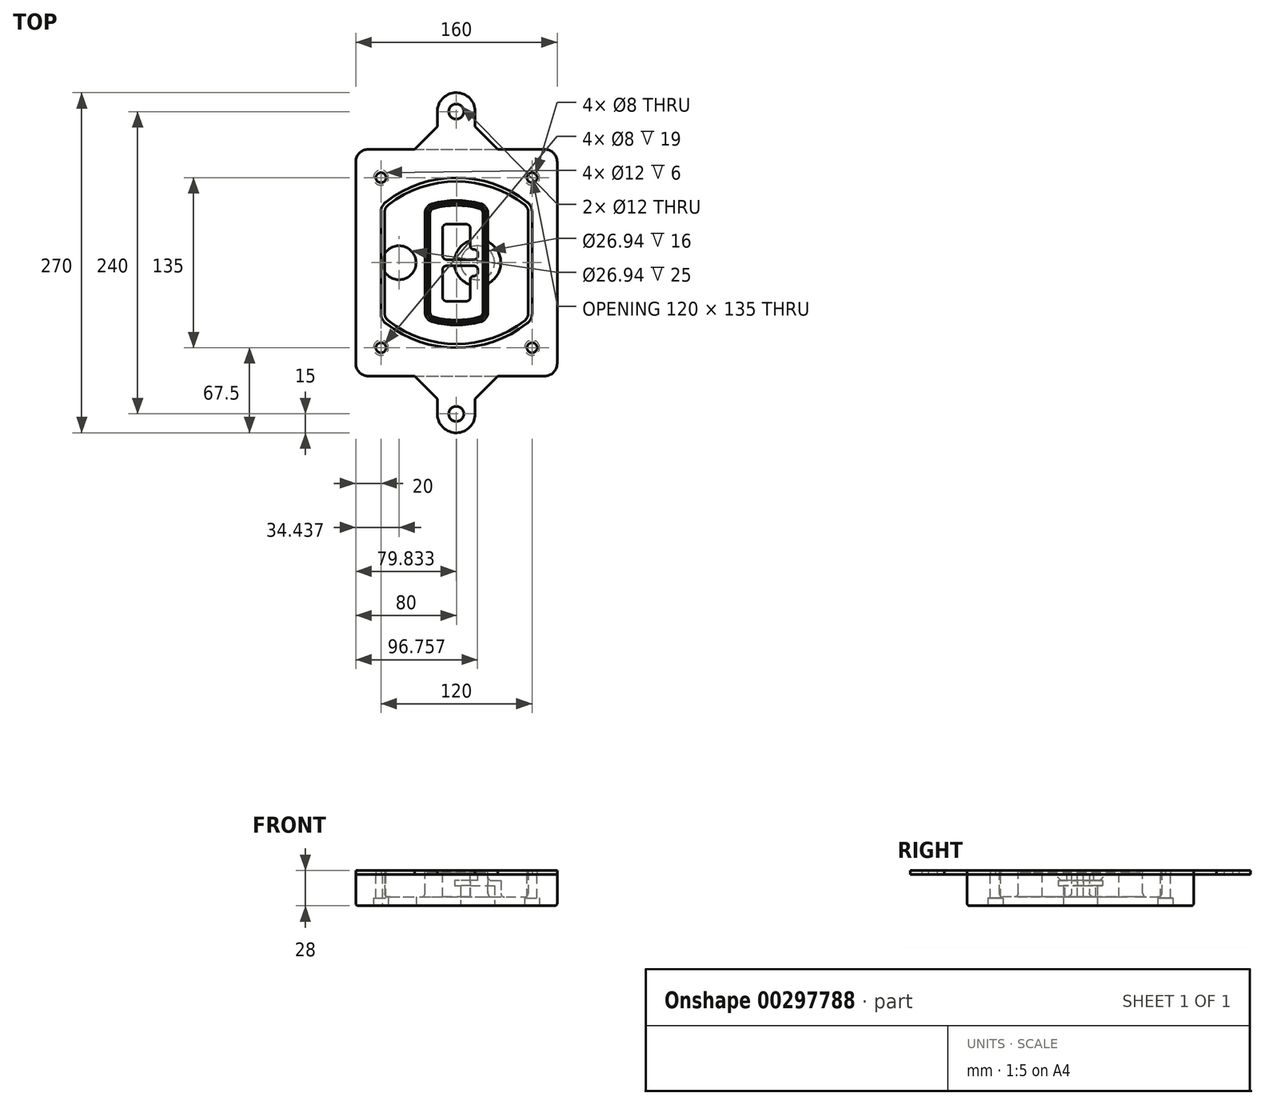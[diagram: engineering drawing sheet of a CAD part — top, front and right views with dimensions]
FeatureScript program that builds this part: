
annotation { "Feature Type Name" : "Feature", "Feature Type Description" : "" }
export const myFeature = defineFeature(function(context is Context, id is Id, definition is map)
    precondition{}
    {
        {
            var Q0;
            Q0=qCreatedBy(makeId("Top.planeOp"),FACE);
            var sketch = newSketch(context, id + "F0", { "sketchPlane" : qUnion([Q0])});
            skPoint(sketch, "E0.rect.middle", {"position": v(0, 0) * mm});
            skLineSegment(sketch, "E1.bottom", {"start": v(-70, -90) * mm, "end": v(70, -90) * mm});
            skLineSegment(sketch, "E1.top", {"start": v(-70, 90) * mm, "end": v(70, 90) * mm});
            skLineSegment(sketch, "E1.left", {"start": v(-80, -80) * mm, "end": v(-80, 80) * mm});
            skLineSegment(sketch, "E1.right", {"start": v(80, -80) * mm, "end": v(80, 80) * mm});
            skLineSegment(sketch, "E2", {"start": v(-80, 90) * mm, "end": v(80, -90) * mm, "construction": true});
            skLineSegment(sketch, "E3", {"start": v(80, 90) * mm, "end": v(-80, -90) * mm, "construction": true});
            skCircle(sketch, "E4", {"center": v(-60, 67.5) * mm, "radius": 4 * mm});
            skCircle(sketch, "E5", {"center": v(60, 67.5) * mm, "radius": 4 * mm});
            skCircle(sketch, "E6", {"center": v(60, -67.5) * mm, "radius": 4 * mm});
            skCircle(sketch, "E7", {"center": v(-60, -67.5) * mm, "radius": 4 * mm});
            skLineSegment(sketch, "E8", {"start": v(-60, 67.5) * mm, "end": v(60, 67.5) * mm, "construction": true});
            skLineSegment(sketch, "E9", {"start": v(60, 67.5) * mm, "end": v(60, -67.5) * mm, "construction": true});
            skLineSegment(sketch, "E10", {"start": v(60, -67.5) * mm, "end": v(-60, -67.5) * mm, "construction": true});
            skLineSegment(sketch, "E11", {"start": v(-60, -67.5) * mm, "end": v(-60, 67.5) * mm, "construction": true});
            skLineSegment(sketch, "E12", {"start": v(-60, 40.3) * mm, "end": v(-60, -40.3) * mm});
            skLineSegment(sketch, "E13", {"start": v(60, 40.3) * mm, "end": v(60, -40.3) * mm});
            skArc(sketch, "E14", {"start": v(56.15, 48.18) * mm, "mid": v(0, 67.5) * mm, "end": v(-56.15, 48.18) * mm});
            skArc(sketch, "E15", {"start": v(-56.15, -48.18) * mm, "mid": v(0, -67.5) * mm, "end": v(56.15, -48.18) * mm});
            skLineSegment(sketch, "E16", {"start": v(-60, 0) * mm, "end": v(60, 0) * mm, "construction": true});
            skPoint(sketch, "E17.visualSharp", {"position": v(-60, -45) * mm});
            skArc(sketch, "E17.filletArc", {"start": v(-60, -40.3) * mm, "mid": v(-58.99, -44.68) * mm, "end": v(-56.15, -48.18) * mm});
            skPoint(sketch, "E18.visualSharp", {"position": v(-60, 45) * mm});
            skArc(sketch, "E18.filletArc", {"start": v(-56.15, 48.18) * mm, "mid": v(-58.99, 44.68) * mm, "end": v(-60, 40.3) * mm});
            skPoint(sketch, "E19.visualSharp", {"position": v(60, 45) * mm});
            skArc(sketch, "E19.filletArc", {"start": v(60, 40.3) * mm, "mid": v(58.99, 44.68) * mm, "end": v(56.15, 48.18) * mm});
            skPoint(sketch, "E20.visualSharp", {"position": v(60, -45) * mm});
            skArc(sketch, "E20.filletArc", {"start": v(56.15, -48.18) * mm, "mid": v(58.99, -44.68) * mm, "end": v(60, -40.3) * mm});
            skPoint(sketch, "E21.visualSharp", {"position": v(-80, 90) * mm});
            skArc(sketch, "E21.filletArc", {"start": v(-70, 90) * mm, "mid": v(-77.07, 87.07) * mm, "end": v(-80, 80) * mm});
            skPoint(sketch, "E22.visualSharp", {"position": v(80, 90) * mm});
            skArc(sketch, "E22.filletArc", {"start": v(80, 80) * mm, "mid": v(77.07, 87.07) * mm, "end": v(70, 90) * mm});
            skPoint(sketch, "E23.visualSharp", {"position": v(80, -90) * mm});
            skArc(sketch, "E23.filletArc", {"start": v(70, -90) * mm, "mid": v(77.07, -87.07) * mm, "end": v(80, -80) * mm});
            skPoint(sketch, "E24.visualSharp", {"position": v(-80, -90) * mm});
            skArc(sketch, "E24.filletArc", {"start": v(-80, -80) * mm, "mid": v(-77.07, -87.07) * mm, "end": v(-70, -90) * mm});
            skArc(sketch, "E25.0", {"start": v(57, 40.3) * mm, "mid": v(56.3, 43.36) * mm, "end": v(54.3, 45.81) * mm});
            skLineSegment(sketch, "E25.1", {"start": v(57, 40.3) * mm, "end": v(57, -40.3) * mm});
            skArc(sketch, "E25.2", {"start": v(54.3, -45.81) * mm, "mid": v(56.3, -43.36) * mm, "end": v(57, -40.3) * mm});
            skArc(sketch, "E25.3", {"start": v(-54.3, -45.81) * mm, "mid": v(0, -64.5) * mm, "end": v(54.3, -45.81) * mm});
            skArc(sketch, "E25.4", {"start": v(-57, -40.3) * mm, "mid": v(-56.3, -43.36) * mm, "end": v(-54.3, -45.81) * mm});
            skArc(sketch, "E25.5", {"start": v(54.3, 45.81) * mm, "mid": v(0, 64.5) * mm, "end": v(-54.3, 45.81) * mm});
            skLineSegment(sketch, "E25.6", {"start": v(-57, 40.3) * mm, "end": v(-57, -40.3) * mm});
            skArc(sketch, "E25.7", {"start": v(-54.3, 45.81) * mm, "mid": v(-56.3, 43.36) * mm, "end": v(-57, 40.3) * mm});
            skArc(sketch, "E26.0", {"start": v(-58.62, 51.33) * mm, "mid": v(-62.58, 46.43) * mm, "end": v(-64, 40.3) * mm});
            skArc(sketch, "E26.1", {"start": v(58.62, 51.33) * mm, "mid": v(0, 71.5) * mm, "end": v(-58.62, 51.33) * mm});
            skArc(sketch, "E26.2", {"start": v(64, 40.3) * mm, "mid": v(62.58, 46.43) * mm, "end": v(58.62, 51.33) * mm});
            skLineSegment(sketch, "E26.3", {"start": v(64, 40.3) * mm, "end": v(64, -40.3) * mm});
            skArc(sketch, "E26.4", {"start": v(58.62, -51.33) * mm, "mid": v(62.58, -46.43) * mm, "end": v(64, -40.3) * mm});
            skLineSegment(sketch, "E26.5", {"start": v(-64, 40.3) * mm, "end": v(-64, -40.3) * mm});
            skArc(sketch, "E26.6", {"start": v(-58.62, -51.33) * mm, "mid": v(0, -71.5) * mm, "end": v(58.62, -51.33) * mm});
            skArc(sketch, "E26.7", {"start": v(-64, -40.3) * mm, "mid": v(-62.58, -46.43) * mm, "end": v(-58.62, -51.33) * mm});
            skSolve(sketch);
        }
        {
            var Q0;
            Q0=makeQuery(id+"F0.imprint","IMPRINT",FACE,{"disambiguationData":[TD([[makeQuery(id+"F0.imprint","IMPRINT",EDGE,{"derivedFrom":sQuery(id+"F0.wireOp",EDGE,"E1.bottom")}),1.0]])]});
            var Q1;
            Q1=makeQuery(id+"F0.imprint","IMPRINT",FACE,{"disambiguationData":[TD([[makeQuery(id+"F0.imprint","IMPRINT",EDGE,{"derivedFrom":sQuery(id+"F0.wireOp",EDGE,"E12")}),1.0]])]});
            var Q2;
            Q2=makeQuery(id+"F0.imprint","IMPRINT",FACE,{"disambiguationData":[TD([[makeQuery(id+"F0.imprint","IMPRINT",EDGE,{"derivedFrom":sQuery(id+"F0.wireOp",EDGE,"E25.0")}),1.0]])]});
            var Q3;
            Q3=makeQuery(id+"F0.imprint","IMPRINT",FACE,{"disambiguationData":[TD([[makeQuery(id+"F0.imprint","IMPRINT",EDGE,{"derivedFrom":sQuery(id+"F0.wireOp",EDGE,"E12")}),-1.0]])]});
            extrude(context, id + "F1", {"entities" : qUnion([Q0, Q1, Q2, Q3]), "oppositeDirection" : true, "depth" : 25 * mm});
        }
        {
            var Q0;
            Q0=makeQuery(id+"F0.imprint","IMPRINT",FACE,{"disambiguationData":[TD([[makeQuery(id+"F0.imprint","IMPRINT",EDGE,{"derivedFrom":sQuery(id+"F0.wireOp",EDGE,"E12")}),1.0]])]});
            extrude(context, id + "F2", {"entities" : qUnion([Q0]), "operationType" : NewBodyOperationType.ADD, "depth" : 3 * mm});
        }
        {
            var Q0;
            Q0=makeQuery(id+"F0.imprint","IMPRINT",FACE,{"disambiguationData":[TD([[makeQuery(id+"F0.imprint","IMPRINT",EDGE,{"derivedFrom":sQuery(id+"F0.wireOp",EDGE,"E25.0")}),1.0]])]});
            extrude(context, id + "F3", {"entities" : qUnion([Q0]), "operationType" : NewBodyOperationType.REMOVE, "oppositeDirection" : true, "depth" : 18 * mm});
        }
        {
            var Q0;
            Q0=makeQuery(id+"F2.opExtrude","CAP_FACE",FACE,{"disambiguationData":[OSD([sQuery(id+"F0.wireOp",EDGE,"E12"),sQuery(id+"F0.wireOp",EDGE,"E13"),sQuery(id+"F0.wireOp",EDGE,"E14"),sQuery(id+"F0.wireOp",EDGE,"E15"),sQuery(id+"F0.wireOp",EDGE,"E17.filletArc"),sQuery(id+"F0.wireOp",EDGE,"E18.filletArc"),sQuery(id+"F0.wireOp",EDGE,"E19.filletArc"),sQuery(id+"F0.wireOp",EDGE,"E20.filletArc"),sQuery(id+"F0.wireOp",EDGE,"E25.0"),sQuery(id+"F0.wireOp",EDGE,"E25.1"),sQuery(id+"F0.wireOp",EDGE,"E25.2"),sQuery(id+"F0.wireOp",EDGE,"E25.3"),sQuery(id+"F0.wireOp",EDGE,"E25.4"),sQuery(id+"F0.wireOp",EDGE,"E25.5"),sQuery(id+"F0.wireOp",EDGE,"E25.6"),sQuery(id+"F0.wireOp",EDGE,"E25.7")])],"isStart":false});
            var sketch = newSketch(context, id + "F4", { "sketchPlane" : qUnion([Q0])});
            skArc(sketch, "E27.0", {"start": v(-19.08, -46.97) * mm, "mid": v(0, -49.5) * mm, "end": v(19.08, -46.97) * mm});
            skArc(sketch, "E28.0", {"start": v(19.08, 46.97) * mm, "mid": v(0, 49.5) * mm, "end": v(-19.08, 46.97) * mm});
            skLineSegment(sketch, "E29", {"start": v(-25, 39.25) * mm, "end": v(-25, -39.25) * mm});
            skLineSegment(sketch, "E30", {"start": v(25, 39.25) * mm, "end": v(25, -39.25) * mm});
            skLineSegment(sketch, "E31", {"start": v(-25, 45.1) * mm, "end": v(25, 45.1) * mm, "construction": true});
            skLineSegment(sketch, "E32", {"start": v(-25, -45.1) * mm, "end": v(25, -45.1) * mm, "construction": true});
            skPoint(sketch, "E33.visualSharp", {"position": v(-25, 45.1) * mm});
            skArc(sketch, "E33.filletArc", {"start": v(-19.08, 46.97) * mm, "mid": v(-23.35, 44.11) * mm, "end": v(-25, 39.25) * mm});
            skPoint(sketch, "E34.visualSharp", {"position": v(25, 45.1) * mm});
            skArc(sketch, "E34.filletArc", {"start": v(25, 39.25) * mm, "mid": v(23.35, 44.11) * mm, "end": v(19.08, 46.97) * mm});
            skPoint(sketch, "E35.visualSharp", {"position": v(25, -45.1) * mm});
            skArc(sketch, "E35.filletArc", {"start": v(19.08, -46.97) * mm, "mid": v(23.35, -44.11) * mm, "end": v(25, -39.25) * mm});
            skPoint(sketch, "E36.visualSharp", {"position": v(-25, -45.1) * mm});
            skArc(sketch, "E36.filletArc", {"start": v(-25, -39.25) * mm, "mid": v(-23.35, -44.11) * mm, "end": v(-19.08, -46.97) * mm});
            skArc(sketch, "E37.0", {"start": v(54.3, 45.81) * mm, "mid": v(0, 64.5) * mm, "end": v(-54.3, 45.81) * mm});
            skArc(sketch, "E37.1", {"start": v(-54.3, 45.81) * mm, "mid": v(-56.3, 43.36) * mm, "end": v(-57, 40.3) * mm});
            skLineSegment(sketch, "E37.2", {"start": v(-57, 40.3) * mm, "end": v(-57, -40.3) * mm});
            skArc(sketch, "E37.3", {"start": v(-57, -40.3) * mm, "mid": v(-56.3, -43.36) * mm, "end": v(-54.3, -45.81) * mm});
            skArc(sketch, "E37.4", {"start": v(-54.3, -45.81) * mm, "mid": v(0, -64.5) * mm, "end": v(54.3, -45.81) * mm});
            skArc(sketch, "E37.5", {"start": v(54.3, -45.81) * mm, "mid": v(56.3, -43.36) * mm, "end": v(57, -40.3) * mm});
            skLineSegment(sketch, "E37.6", {"start": v(57, 40.3) * mm, "end": v(57, -40.3) * mm});
            skArc(sketch, "E37.7", {"start": v(57, 40.3) * mm, "mid": v(56.3, 43.36) * mm, "end": v(54.3, 45.81) * mm});
            skLineSegment(sketch, "E38.0", {"start": v(23, 39.25) * mm, "end": v(23, -39.25) * mm});
            skArc(sketch, "E38.1", {"start": v(18.56, -45.04) * mm, "mid": v(21.76, -42.9) * mm, "end": v(23, -39.25) * mm});
            skArc(sketch, "E38.2", {"start": v(-18.56, -45.04) * mm, "mid": v(0, -47.5) * mm, "end": v(18.56, -45.04) * mm});
            skArc(sketch, "E38.3", {"start": v(-23, -39.25) * mm, "mid": v(-21.76, -42.9) * mm, "end": v(-18.56, -45.04) * mm});
            skLineSegment(sketch, "E38.4", {"start": v(-23, 39.25) * mm, "end": v(-23, -39.25) * mm});
            skArc(sketch, "E38.5", {"start": v(23, 39.25) * mm, "mid": v(21.76, 42.9) * mm, "end": v(18.56, 45.04) * mm});
            skArc(sketch, "E38.6", {"start": v(-18.56, 45.04) * mm, "mid": v(-21.76, 42.9) * mm, "end": v(-23, 39.25) * mm});
            skArc(sketch, "E38.7", {"start": v(18.56, 45.04) * mm, "mid": v(0, 47.5) * mm, "end": v(-18.56, 45.04) * mm});
            skArc(sketch, "E39.0", {"start": v(21, 39.25) * mm, "mid": v(20.18, 41.68) * mm, "end": v(18.04, 43.1) * mm});
            skLineSegment(sketch, "E39.1", {"start": v(21, 39.25) * mm, "end": v(21, -39.25) * mm});
            skArc(sketch, "E39.2", {"start": v(18.04, -43.1) * mm, "mid": v(20.18, -41.68) * mm, "end": v(21, -39.25) * mm});
            skArc(sketch, "E39.3", {"start": v(-18.04, -43.1) * mm, "mid": v(0, -45.5) * mm, "end": v(18.04, -43.1) * mm});
            skArc(sketch, "E39.4", {"start": v(-21, -39.25) * mm, "mid": v(-20.18, -41.68) * mm, "end": v(-18.04, -43.1) * mm});
            skArc(sketch, "E39.5", {"start": v(18.04, 43.1) * mm, "mid": v(0, 45.5) * mm, "end": v(-18.04, 43.1) * mm});
            skLineSegment(sketch, "E39.6", {"start": v(-21, 39.25) * mm, "end": v(-21, -39.25) * mm});
            skArc(sketch, "E39.7", {"start": v(-18.04, 43.1) * mm, "mid": v(-20.18, 41.68) * mm, "end": v(-21, 39.25) * mm});
            skLineSegment(sketch, "E40", {"start": v(-25, 0) * mm, "end": v(25, 0) * mm, "construction": true});
            skLineSegment(sketch, "E41", {"start": v(-11, 5.5) * mm, "end": v(-11, 27.5) * mm});
            skLineSegment(sketch, "E42", {"start": v(-8, 30.5) * mm, "end": v(8, 30.5) * mm});
            skLineSegment(sketch, "E43", {"start": v(11, 27.5) * mm, "end": v(11, 13.5) * mm});
            skLineSegment(sketch, "E44", {"start": v(14, 10.5) * mm, "end": v(14, 10.5) * mm});
            skLineSegment(sketch, "E45", {"start": v(17, 7.5) * mm, "end": v(17, 5.5) * mm});
            skLineSegment(sketch, "E46", {"start": v(14, 2.5) * mm, "end": v(-8, 2.5) * mm});
            skPoint(sketch, "E47.visualSharp", {"position": v(-11, 30.5) * mm});
            skArc(sketch, "E47.filletArc", {"start": v(-8, 30.5) * mm, "mid": v(-10.12, 29.62) * mm, "end": v(-11, 27.5) * mm});
            skPoint(sketch, "E48.visualSharp", {"position": v(11, 30.5) * mm});
            skArc(sketch, "E48.filletArc", {"start": v(11, 27.5) * mm, "mid": v(10.12, 29.62) * mm, "end": v(8, 30.5) * mm});
            skPoint(sketch, "E49.visualSharp", {"position": v(11, 10.5) * mm});
            skArc(sketch, "E49.filletArc", {"start": v(11, 13.5) * mm, "mid": v(11.88, 11.38) * mm, "end": v(14, 10.5) * mm});
            skPoint(sketch, "E50.visualSharp", {"position": v(17, 10.5) * mm});
            skArc(sketch, "E50.filletArc", {"start": v(17, 7.5) * mm, "mid": v(16.12, 9.62) * mm, "end": v(14, 10.5) * mm});
            skPoint(sketch, "E51.visualSharp", {"position": v(17, 2.5) * mm});
            skArc(sketch, "E51.filletArc", {"start": v(14, 2.5) * mm, "mid": v(16.12, 3.38) * mm, "end": v(17, 5.5) * mm});
            skPoint(sketch, "E52.visualSharp", {"position": v(-11, 2.5) * mm});
            skArc(sketch, "E52.filletArc", {"start": v(-11, 5.5) * mm, "mid": v(-10.12, 3.38) * mm, "end": v(-8, 2.5) * mm});
            skLineSegment(sketch, "E53.0.MirrorCS", {"start": v(14, -2.5) * mm, "end": v(-8, -2.5) * mm});
            skArc(sketch, "E54.0.MirrorCS", {"start": v(-11, -5.5) * mm, "mid": v(-10.12, -3.38) * mm, "end": v(-8, -2.5) * mm});
            skLineSegment(sketch, "E55.0.MirrorCS", {"start": v(-11, -5.5) * mm, "end": v(-11, -27.5) * mm});
            skArc(sketch, "E56.0.MirrorCS", {"start": v(-8, -30.5) * mm, "mid": v(-10.12, -29.62) * mm, "end": v(-11, -27.5) * mm});
            skLineSegment(sketch, "E57.0.MirrorCS", {"start": v(-8, -30.5) * mm, "end": v(8, -30.5) * mm});
            skArc(sketch, "E58.0.MirrorCS", {"start": v(11, -27.5) * mm, "mid": v(10.12, -29.62) * mm, "end": v(8, -30.5) * mm});
            skLineSegment(sketch, "E59.0.MirrorCS", {"start": v(11, -27.5) * mm, "end": v(11, -13.5) * mm});
            skArc(sketch, "E60.0.MirrorCS", {"start": v(11, -13.5) * mm, "mid": v(11.88, -11.38) * mm, "end": v(14, -10.5) * mm});
            skArc(sketch, "E61.0.MirrorCS", {"start": v(17, -7.5) * mm, "mid": v(16.12, -9.62) * mm, "end": v(14, -10.5) * mm});
            skLineSegment(sketch, "E62.0.MirrorCS", {"start": v(17, -7.5) * mm, "end": v(17, -5.5) * mm});
            skArc(sketch, "E63.0.MirrorCS", {"start": v(14, -2.5) * mm, "mid": v(16.12, -3.38) * mm, "end": v(17, -5.5) * mm});
            skSolve(sketch);
        }
        {
            var Q0;
            Q0=makeQuery(id+"F4.imprint","IMPRINT",FACE,{"disambiguationData":[TD([[makeQuery(id+"F4.imprint","IMPRINT",EDGE,{"derivedFrom":sQuery(id+"F4.wireOp",EDGE,"E27.0")}),1.0]])]});
            var Q1;
            Q1=makeQuery(id+"F4.imprint","IMPRINT",FACE,{"disambiguationData":[TD([[makeQuery(id+"F4.imprint","IMPRINT",EDGE,{"derivedFrom":sQuery(id+"F4.wireOp",EDGE,"E38.0")}),-1.0]])]});
            var Q2;
            Q2=makeQuery(id+"F4.imprint","IMPRINT",FACE,{"disambiguationData":[TD([[makeQuery(id+"F4.imprint","IMPRINT",EDGE,{"derivedFrom":sQuery(id+"F4.wireOp",EDGE,"E39.0")}),1.0]])]});
            extrude(context, id + "F5", {"entities" : qUnion([Q0, Q1, Q2]), "operationType" : NewBodyOperationType.ADD, "endBound" : BoundingType.UP_TO_NEXT, "oppositeDirection" : true, "depth" : 25 * mm});
        }
        {
            var Q0;
            Q0=makeQuery(id+"F4.imprint","IMPRINT",FACE,{"disambiguationData":[TD([[makeQuery(id+"F4.imprint","IMPRINT",EDGE,{"derivedFrom":sQuery(id+"F4.wireOp",EDGE,"E38.0")}),-1.0]])]});
            extrude(context, id + "F6", {"entities" : qUnion([Q0]), "operationType" : NewBodyOperationType.REMOVE, "oppositeDirection" : true, "depth" : 2 * mm});
        }
        {
            var Q0;
            Q0=makeQuery(id+"F1.opExtrude","CAP_FACE",FACE,{"disambiguationData":[OSD([sQuery(id+"F0.wireOp",EDGE,"E1.bottom"),sQuery(id+"F0.wireOp",EDGE,"E1.top"),sQuery(id+"F0.wireOp",EDGE,"E1.left"),sQuery(id+"F0.wireOp",EDGE,"E1.right"),sQuery(id+"F0.wireOp",EDGE,"E4"),sQuery(id+"F0.wireOp",EDGE,"E5"),sQuery(id+"F0.wireOp",EDGE,"E6"),sQuery(id+"F0.wireOp",EDGE,"E7"),sQuery(id+"F0.wireOp",EDGE,"E21.filletArc"),sQuery(id+"F0.wireOp",EDGE,"E22.filletArc"),sQuery(id+"F0.wireOp",EDGE,"E23.filletArc"),sQuery(id+"F0.wireOp",EDGE,"E24.filletArc")])],"isStart":false});
            var sketch = newSketch(context, id + "F7", { "sketchPlane" : qUnion([Q0])});
            skCircle(sketch, "E64", {"center": v(16.76, 0) * mm, "radius": 13.47 * mm});
            skCircle(sketch, "E65", {"center": v(-45.56, 0) * mm, "radius": 13.47 * mm});
            skLineSegment(sketch, "E66", {"start": v(80, 0) * mm, "end": v(-80, 0) * mm});
            skCircle(sketch, "E67", {"center": v(16.76, 0) * mm, "radius": 18.47 * mm});
            skCircle(sketch, "E68", {"center": v(60, -67.5) * mm, "radius": 6 * mm});
            skCircle(sketch, "E69", {"center": v(-60, -67.5) * mm, "radius": 6 * mm});
            skCircle(sketch, "E70", {"center": v(-60, 67.5) * mm, "radius": 6 * mm});
            skCircle(sketch, "E71", {"center": v(60, 67.5) * mm, "radius": 6 * mm});
            skSolve(sketch);
        }
        {
            var Q0;
            {var subQ1=sQuery(id+"F7.wireOp",EDGE,"E66");var subQ4=sQuery(id+"F7.wireOp",EDGE,"E64");var subQ6=makeQuery(id+"F7.imprint","INTERSECT",VERTEX,{"disambiguationData":[OD(0.0)],"derivedFrom":[subQ4,subQ1]});Q0=makeQuery(id+"F7.imprint","IMPRINT",FACE,{"disambiguationData":[TD([[makeQuery(id+"F7.imprint","IMPRINT",EDGE,{"disambiguationData":[TD([[subQ6,-1.0]])],"derivedFrom":subQ4}),-1.0]])]});}
            var Q1;
            {var subQ0=sQuery(id+"F7.wireOp",EDGE,"E66");var subQ1=sQuery(id+"F7.wireOp",EDGE,"E64");var subQ3=makeQuery(id+"F7.imprint","INTERSECT",VERTEX,{"disambiguationData":[OD(0.0)],"derivedFrom":[subQ1,subQ0]});Q1=makeQuery(id+"F7.imprint","IMPRINT",FACE,{"disambiguationData":[TD([[makeQuery(id+"F7.imprint","IMPRINT",EDGE,{"disambiguationData":[TD([[subQ3,-1.0]])],"derivedFrom":subQ1}),1.0]])]});}
            var Q2;
            {var subQ0=sQuery(id+"F7.wireOp",EDGE,"E66");var subQ1=sQuery(id+"F7.wireOp",EDGE,"E64");var subQ3=makeQuery(id+"F7.imprint","INTERSECT",VERTEX,{"disambiguationData":[OD(0.0)],"derivedFrom":[subQ1,subQ0]});Q2=makeQuery(id+"F7.imprint","IMPRINT",FACE,{"disambiguationData":[TD([[makeQuery(id+"F7.imprint","IMPRINT",EDGE,{"disambiguationData":[TD([[subQ3,1.0]])],"derivedFrom":subQ1}),1.0]])]});}
            var Q3;
            {var subQ1=sQuery(id+"F7.wireOp",EDGE,"E66");var subQ4=sQuery(id+"F7.wireOp",EDGE,"E64");var subQ6=makeQuery(id+"F7.imprint","INTERSECT",VERTEX,{"disambiguationData":[OD(0.0)],"derivedFrom":[subQ4,subQ1]});Q3=makeQuery(id+"F7.imprint","IMPRINT",FACE,{"disambiguationData":[TD([[makeQuery(id+"F7.imprint","IMPRINT",EDGE,{"disambiguationData":[TD([[subQ6,1.0]])],"derivedFrom":subQ4}),-1.0]])]});}
            extrude(context, id + "F8", {"entities" : qUnion([Q0, Q1, Q2, Q3]), "operationType" : NewBodyOperationType.ADD, "oppositeDirection" : true, "depth" : 20 * mm});
        }
        {
            var Q0;
            {var subQ0=sQuery(id+"F7.wireOp",EDGE,"E66");var subQ1=sQuery(id+"F7.wireOp",EDGE,"E64");var subQ3=makeQuery(id+"F7.imprint","INTERSECT",VERTEX,{"disambiguationData":[OD(0.0)],"derivedFrom":[subQ1,subQ0]});Q0=makeQuery(id+"F7.imprint","IMPRINT",FACE,{"disambiguationData":[TD([[makeQuery(id+"F7.imprint","IMPRINT",EDGE,{"disambiguationData":[TD([[subQ3,-1.0]])],"derivedFrom":subQ1}),1.0]])]});}
            var Q1;
            {var subQ0=sQuery(id+"F7.wireOp",EDGE,"E66");var subQ1=sQuery(id+"F7.wireOp",EDGE,"E64");var subQ3=makeQuery(id+"F7.imprint","INTERSECT",VERTEX,{"disambiguationData":[OD(0.0)],"derivedFrom":[subQ1,subQ0]});Q1=makeQuery(id+"F7.imprint","IMPRINT",FACE,{"disambiguationData":[TD([[makeQuery(id+"F7.imprint","IMPRINT",EDGE,{"disambiguationData":[TD([[subQ3,1.0]])],"derivedFrom":subQ1}),1.0]])]});}
            extrude(context, id + "F9", {"entities" : qUnion([Q0, Q1]), "operationType" : NewBodyOperationType.REMOVE, "oppositeDirection" : true, "depth" : 16 * mm});
        }
        {
            var Q0;
            {var subQ0=sQuery(id+"F7.wireOp",EDGE,"E66");var subQ1=sQuery(id+"F7.wireOp",EDGE,"E65");var subQ3=makeQuery(id+"F7.imprint","INTERSECT",VERTEX,{"disambiguationData":[OD(0.0)],"derivedFrom":[subQ1,subQ0]});Q0=makeQuery(id+"F7.imprint","IMPRINT",FACE,{"disambiguationData":[TD([[makeQuery(id+"F7.imprint","IMPRINT",EDGE,{"disambiguationData":[TD([[subQ3,-1.0]])],"derivedFrom":subQ1}),1.0]])]});}
            var Q1;
            {var subQ0=sQuery(id+"F7.wireOp",EDGE,"E66");var subQ1=sQuery(id+"F7.wireOp",EDGE,"E65");var subQ3=makeQuery(id+"F7.imprint","INTERSECT",VERTEX,{"disambiguationData":[OD(0.0)],"derivedFrom":[subQ1,subQ0]});Q1=makeQuery(id+"F7.imprint","IMPRINT",FACE,{"disambiguationData":[TD([[makeQuery(id+"F7.imprint","IMPRINT",EDGE,{"disambiguationData":[TD([[subQ3,1.0]])],"derivedFrom":subQ1}),1.0]])]});}
            extrude(context, id + "F10", {"entities" : qUnion([Q0, Q1]), "operationType" : NewBodyOperationType.REMOVE, "oppositeDirection" : true, "depth" : 25 * mm});
        }
        {
            var Q0;
            Q0=makeQuery(id+"F7.imprint","IMPRINT",FACE,{"disambiguationData":[TD([[makeQuery(id+"F7.imprint","IMPRINT",EDGE,{"derivedFrom":sQuery(id+"F7.wireOp",EDGE,"E68")}),1.0]])]});
            var Q1;
            Q1=makeQuery(id+"F7.imprint","IMPRINT",FACE,{"disambiguationData":[TD([[makeQuery(id+"F7.imprint","IMPRINT",EDGE,{"derivedFrom":makeQuery(id+"F1.opExtrude","CAP_EDGE",EDGE,{"disambiguationData":[OSD([sQuery(id+"F0.wireOp",EDGE,"E5")])],"isStart":false})}),-1.0]])]});
            var Q2;
            Q2=makeQuery(id+"F7.imprint","IMPRINT",FACE,{"disambiguationData":[TD([[makeQuery(id+"F7.imprint","IMPRINT",EDGE,{"derivedFrom":sQuery(id+"F7.wireOp",EDGE,"E69")}),1.0]])]});
            var Q3;
            Q3=makeQuery(id+"F7.imprint","IMPRINT",FACE,{"disambiguationData":[TD([[makeQuery(id+"F7.imprint","IMPRINT",EDGE,{"derivedFrom":makeQuery(id+"F1.opExtrude","CAP_EDGE",EDGE,{"disambiguationData":[OSD([sQuery(id+"F0.wireOp",EDGE,"E4")])],"isStart":false})}),-1.0]])]});
            var Q4;
            Q4=makeQuery(id+"F7.imprint","IMPRINT",FACE,{"disambiguationData":[TD([[makeQuery(id+"F7.imprint","IMPRINT",EDGE,{"derivedFrom":sQuery(id+"F7.wireOp",EDGE,"E70")}),1.0]])]});
            var Q5;
            Q5=makeQuery(id+"F7.imprint","IMPRINT",FACE,{"disambiguationData":[TD([[makeQuery(id+"F7.imprint","IMPRINT",EDGE,{"derivedFrom":makeQuery(id+"F1.opExtrude","CAP_EDGE",EDGE,{"disambiguationData":[OSD([sQuery(id+"F0.wireOp",EDGE,"E7")])],"isStart":false})}),-1.0]])]});
            var Q6;
            Q6=makeQuery(id+"F7.imprint","IMPRINT",FACE,{"disambiguationData":[TD([[makeQuery(id+"F7.imprint","IMPRINT",EDGE,{"derivedFrom":sQuery(id+"F7.wireOp",EDGE,"E71")}),1.0]])]});
            var Q7;
            Q7=makeQuery(id+"F7.imprint","IMPRINT",FACE,{"disambiguationData":[TD([[makeQuery(id+"F7.imprint","IMPRINT",EDGE,{"derivedFrom":makeQuery(id+"F1.opExtrude","CAP_EDGE",EDGE,{"disambiguationData":[OSD([sQuery(id+"F0.wireOp",EDGE,"E6")])],"isStart":false})}),-1.0]])]});
            extrude(context, id + "F11", {"entities" : qUnion([Q0, Q1, Q2, Q3, Q4, Q5, Q6, Q7]), "operationType" : NewBodyOperationType.REMOVE, "oppositeDirection" : true, "depth" : 6 * mm});
        }
        {
            var Q0;
            Q0=makeQuery(id+"F9.boolean.opBoolean","COPY",FACE,{"derivedFrom":makeQuery(id+"F9.opExtrude","CAP_FACE",FACE,{"disambiguationData":[OSD([sQuery(id+"F7.wireOp",EDGE,"E64")])],"isStart":false})});
            var sketch = newSketch(context, id + "F12", { "sketchPlane" : qUnion([Q0])});
            skArc(sketch, "E72.0", {"start": v(11, 17.55) * mm, "mid": v(2.57, 11.82) * mm, "end": v(-1.54, 2.5) * mm});
            skArc(sketch, "E72.1", {"start": v(-1.54, -2.5) * mm, "mid": v(2.57, -11.82) * mm, "end": v(11, -17.55) * mm});
            skLineSegment(sketch, "E73", {"start": v(-1.54, -2.5) * mm, "end": v(14, -2.5) * mm});
            skLineSegment(sketch, "E74.0", {"start": v(14, 2.5) * mm, "end": v(-1.54, 2.5) * mm});
            skArc(sketch, "E74.1", {"start": v(14, 2.5) * mm, "mid": v(16.12, 3.38) * mm, "end": v(17, 5.5) * mm});
            skLineSegment(sketch, "E74.2", {"start": v(17, 7.5) * mm, "end": v(17, 5.5) * mm});
            skArc(sketch, "E74.3", {"start": v(17, 7.5) * mm, "mid": v(16.12, 9.62) * mm, "end": v(14, 10.5) * mm});
            skArc(sketch, "E74.4", {"start": v(11, 13.5) * mm, "mid": v(11.88, 11.38) * mm, "end": v(14, 10.5) * mm});
            skLineSegment(sketch, "E74.5", {"start": v(11, 17.55) * mm, "end": v(11, 13.5) * mm});
            skLineSegment(sketch, "E74.7", {"start": v(14, -2.5) * mm, "end": v(-1.54, -2.5) * mm});
            skArc(sketch, "E74.8", {"start": v(14, -2.5) * mm, "mid": v(16.12, -3.38) * mm, "end": v(17, -5.5) * mm});
            skLineSegment(sketch, "E74.9", {"start": v(17, -7.5) * mm, "end": v(17, -5.5) * mm});
            skArc(sketch, "E74.10", {"start": v(17, -7.5) * mm, "mid": v(16.12, -9.62) * mm, "end": v(14, -10.5) * mm});
            skArc(sketch, "E74.11", {"start": v(11, -13.5) * mm, "mid": v(11.88, -11.38) * mm, "end": v(14, -10.5) * mm});
            skLineSegment(sketch, "E74.12", {"start": v(11, -17.55) * mm, "end": v(11, -13.5) * mm});
            skPoint(sketch, "E75.orphan", {"position": v(11, -27.5) * mm});
            skPoint(sketch, "E76.orphan", {"position": v(-8, -2.5) * mm});
            skPoint(sketch, "E77.orphan", {"position": v(-8, 2.5) * mm});
            skPoint(sketch, "E78.orphan", {"position": v(11, 27.5) * mm});
            skSolve(sketch);
        }
        {
            var Q0;
            {var subQ7=sQuery(id+"F12.wireOp",EDGE,"E72.0");var subQ14=sQuery(id+"F12.wireOp",EDGE,"E72.1");var subQ16=sQuery(id+"F12.wireOp",EDGE,"E74.1");var subQ18=sQuery(id+"F12.wireOp",EDGE,"E74.8");Q0=qUnion([makeQuery(id+"F12.imprint","IMPRINT",FACE,{"disambiguationData":[TD([[makeQuery(id+"F12.imprint","IMPRINT",EDGE,{"derivedFrom":subQ7}),1.0]])]}),makeQuery(id+"F12.imprint","IMPRINT",FACE,{"disambiguationData":[TD([[makeQuery(id+"F12.imprint","IMPRINT",EDGE,{"derivedFrom":subQ14}),1.0]])]}),makeQuery(id+"F12.imprint","IMPRINT",FACE,{"disambiguationData":[TD([[makeQuery(id+"F12.imprint","IMPRINT",EDGE,{"derivedFrom":subQ16}),1.0]])]}),makeQuery(id+"F12.imprint","IMPRINT",FACE,{"disambiguationData":[TD([[makeQuery(id+"F12.imprint","IMPRINT",EDGE,{"derivedFrom":subQ18}),-1.0]])]})]);}
            var Q1;
            Q1=makeQuery(id+"F5.boolean.opBoolean","SPLIT",FACE,{"disambiguationData":[TD([makeQuery(id+"F5.opExtrude","SWEPT_FACE",FACE,{"disambiguationData":[OSD([sQuery(id+"F4.wireOp",EDGE,"E41")])]})])],"derivedFrom":makeQuery(id+"F3.boolean.opBoolean","COPY",FACE,{"derivedFrom":makeQuery(id+"F3.opExtrude","CAP_FACE",FACE,{"disambiguationData":[OSD([sQuery(id+"F0.wireOp",EDGE,"E25.0"),sQuery(id+"F0.wireOp",EDGE,"E25.1"),sQuery(id+"F0.wireOp",EDGE,"E25.2"),sQuery(id+"F0.wireOp",EDGE,"E25.3"),sQuery(id+"F0.wireOp",EDGE,"E25.4"),sQuery(id+"F0.wireOp",EDGE,"E25.5"),sQuery(id+"F0.wireOp",EDGE,"E25.6"),sQuery(id+"F0.wireOp",EDGE,"E25.7")])],"isStart":false})})});
            extrude(context, id + "F13", {"entities" : qUnion([Q0]), "operationType" : NewBodyOperationType.REMOVE, "endBound" : BoundingType.UP_TO_SURFACE, "endBoundEntityFace" : qUnion([Q1]), "depth" : 25 * mm});
        }
        {
            var Q0;
            Q0=makeQuery(id+"F3.boolean.opBoolean","COPY",EDGE,{"derivedFrom":makeQuery(id+"F3.opExtrude","CAP_EDGE",EDGE,{"disambiguationData":[OSD([sQuery(id+"F0.wireOp",EDGE,"E25.6")])],"isStart":false})});
            var Q1;
            Q1=makeQuery(id+"F8.boolean.opBoolean","INTERSECT",EDGE,{"derivedFrom":[makeQuery(id+"F5.opExtrude","SWEPT_FACE",FACE,{"disambiguationData":[OSD([sQuery(id+"F4.wireOp",EDGE,"E30")])]}),makeQuery(id+"F8.opExtrude","CAP_FACE",FACE,{"disambiguationData":[OSD([sQuery(id+"F7.wireOp",EDGE,"E67")])],"isStart":false})]});
            var Q2;
            Q2=makeQuery(id+"F8.boolean.opBoolean","INTERSECT",EDGE,{"disambiguationData":[OD(1.0)],"derivedFrom":[makeQuery(id+"F5.opExtrude","SWEPT_FACE",FACE,{"disambiguationData":[OSD([sQuery(id+"F4.wireOp",EDGE,"E30")])]}),makeQuery(id+"F8.opExtrude","SWEPT_FACE",FACE,{"disambiguationData":[OSD([sQuery(id+"F7.wireOp",EDGE,"E67")])]})]});
            var Q3;
            {var subQ0=sQuery(id+"F4.wireOp",EDGE,"E30");Q3=makeQuery(id+"F8.boolean.opBoolean","SPLIT",EDGE,{"disambiguationData":[TD([makeQuery(id+"F5.opExtrude","SWEPT_FACE",FACE,{"disambiguationData":[OSD([sQuery(id+"F4.wireOp",EDGE,"E35.filletArc")])]})])],"derivedFrom":makeQuery(id+"F5.opExtrude","CAP_EDGE",EDGE,{"disambiguationData":[OSD([subQ0])],"isStart":false})});}
            var Q4;
            {var subQ0=sQuery(id+"F0.wireOp",EDGE,"E25.7");var subQ1=sQuery(id+"F0.wireOp",EDGE,"E25.1");var subQ2=sQuery(id+"F0.wireOp",EDGE,"E25.6");var subQ3=sQuery(id+"F0.wireOp",EDGE,"E25.5");var subQ4=sQuery(id+"F0.wireOp",EDGE,"E25.4");var subQ5=sQuery(id+"F0.wireOp",EDGE,"E25.0");var subQ6=sQuery(id+"F0.wireOp",EDGE,"E25.2");var subQ7=sQuery(id+"F0.wireOp",EDGE,"E25.3");Q4=makeQuery(id+"F8.boolean.opBoolean","INTERSECT",EDGE,{"derivedFrom":[makeQuery(id+"F5.boolean.opBoolean","SPLIT",FACE,{"disambiguationData":[TD([makeQuery(id+"F2.opExtrude","SWEPT_FACE",FACE,{"disambiguationData":[OSD([subQ5])]})])],"derivedFrom":makeQuery(id+"F3.boolean.opBoolean","COPY",FACE,{"derivedFrom":makeQuery(id+"F3.opExtrude","CAP_FACE",FACE,{"disambiguationData":[OSD([subQ5,subQ1,subQ6,subQ7,subQ4,subQ3,subQ2,subQ0])],"isStart":false})})}),makeQuery(id+"F8.opExtrude","SWEPT_FACE",FACE,{"disambiguationData":[OSD([sQuery(id+"F7.wireOp",EDGE,"E67")])]})]});}
            var Q5;
            Q5=makeQuery(id+"F8.boolean.opBoolean","INTERSECT",EDGE,{"disambiguationData":[OD(0.0)],"derivedFrom":[makeQuery(id+"F5.opExtrude","SWEPT_FACE",FACE,{"disambiguationData":[OSD([sQuery(id+"F4.wireOp",EDGE,"E30")])]}),makeQuery(id+"F8.opExtrude","SWEPT_FACE",FACE,{"disambiguationData":[OSD([sQuery(id+"F7.wireOp",EDGE,"E67")])]})]});
            fillet(context, id + "F14", {"entities" : qUnion([Q0, Q1, Q2, Q3, Q4, Q5]), "radius" : 3 * mm, "tangentPropagation" : true, "allowEdgeOverflow" : false});
        }
        {
            var Q0;
            Q0=makeQuery(id+"F1.opExtrude","CAP_EDGE",EDGE,{"disambiguationData":[OSD([sQuery(id+"F0.wireOp",EDGE,"E1.bottom")])],"isStart":false});
            fillet(context, id + "F15", {"entities" : qUnion([Q0]), "radius" : 2 * mm, "tangentPropagation" : true, "allowEdgeOverflow" : false});
        }
        {
            var Q0;
            {var subQ0=sQuery(id+"F0.wireOp",EDGE,"E21.filletArc");var subQ1=sQuery(id+"F0.wireOp",EDGE,"E7");var subQ2=sQuery(id+"F0.wireOp",EDGE,"E6");var subQ3=sQuery(id+"F0.wireOp",EDGE,"E5");var subQ4=sQuery(id+"F0.wireOp",EDGE,"E4");var subQ5=sQuery(id+"F0.wireOp",EDGE,"E22.filletArc");var subQ6=sQuery(id+"F0.wireOp",EDGE,"E1.bottom");var subQ7=sQuery(id+"F0.wireOp",EDGE,"E1.right");var subQ8=sQuery(id+"F0.wireOp",EDGE,"E1.top");var subQ9=sQuery(id+"F0.wireOp",EDGE,"E1.left");var subQ10=sQuery(id+"F0.wireOp",EDGE,"E23.filletArc");var subQ11=sQuery(id+"F0.wireOp",EDGE,"E24.filletArc");Q0=makeQuery(id+"F2.boolean.opBoolean","SPLIT",FACE,{"disambiguationData":[TD([makeQuery(id+"F1.opExtrude","SWEPT_FACE",FACE,{"disambiguationData":[OSD([subQ6])]})])],"derivedFrom":makeQuery(id+"F1.opExtrude","CAP_FACE",FACE,{"disambiguationData":[OSD([subQ6,subQ8,subQ9,subQ7,subQ4,subQ3,subQ2,subQ1,subQ0,subQ5,subQ10,subQ11])],"isStart":true})});}
            var sketch = newSketch(context, id + "F16", { "sketchPlane" : qUnion([Q0])});
            skLineSegment(sketch, "E79", {"start": v(-33.15, 90) * mm, "end": v(-15.15, 108) * mm});
            skLineSegment(sketch, "E80", {"start": v(-15.15, 108) * mm, "end": v(-15.15, 108.08) * mm});
            skLineSegment(sketch, "E81", {"start": v(32.83, 90) * mm, "end": v(14.83, 108) * mm});
            skLineSegment(sketch, "E82", {"start": v(14.83, 108) * mm, "end": v(14.83, 108.08) * mm});
            skLineSegment(sketch, "E83", {"start": v(-80, 0) * mm, "end": v(80, 0) * mm, "construction": true});
            skLineSegment(sketch, "E84.MirrorCS", {"start": v(-15.15, -108) * mm, "end": v(-15.15, -108.08) * mm});
            skLineSegment(sketch, "E85.MirrorCS", {"start": v(14.83, -108) * mm, "end": v(14.83, -108.08) * mm});
            skLineSegment(sketch, "E86", {"start": v(-15.15, 108) * mm, "end": v(-15.15, 120.67) * mm});
            skLineSegment(sketch, "E87", {"start": v(14.83, 108.08) * mm, "end": v(14.83, 120) * mm});
            skArc(sketch, "E88", {"start": v(14.83, 120) * mm, "mid": v(0.17, 135) * mm, "end": v(-15.15, 120.67) * mm});
            skLineSegment(sketch, "E89", {"start": v(-0.17, 120) * mm, "end": v(0, 0) * mm, "construction": true});
            skCircle(sketch, "E90", {"center": v(-0.17, 120) * mm, "radius": 6 * mm});
            skLineSegment(sketch, "E91.MirrorCS", {"start": v(-33.15, -90) * mm, "end": v(-15.15, -108) * mm});
            skLineSegment(sketch, "E92.MirrorCS", {"start": v(-15.15, -108) * mm, "end": v(-15.15, -120.67) * mm});
            skArc(sketch, "E93.MirrorCS", {"start": v(14.83, -120) * mm, "mid": v(0.17, -135) * mm, "end": v(-15.15, -120.67) * mm});
            skLineSegment(sketch, "E94.MirrorCS", {"start": v(14.83, -108.08) * mm, "end": v(14.83, -120) * mm});
            skLineSegment(sketch, "E95.MirrorCS", {"start": v(32.83, -90) * mm, "end": v(14.83, -108) * mm});
            skLineSegment(sketch, "E96.MirrorCS", {"start": v(-0.17, -120) * mm, "end": v(0, 0) * mm, "construction": true});
            skCircle(sketch, "E97.MirrorC", {"center": v(-0.17, -120) * mm, "radius": 6 * mm});
            skSolve(sketch);
        }
        {
            var Q0;
            {var subQ3=sQuery(id+"F16.wireOp",EDGE,"E79");Q0=makeQuery(id+"F16.imprint","IMPRINT",FACE,{"disambiguationData":[TD([[makeQuery(id+"F16.imprint","IMPRINT",EDGE,{"derivedFrom":subQ3}),-1.0]])]});}
            var Q1;
            {var subQ3=sQuery(id+"F16.wireOp",EDGE,"44fc6be7-808d-41b7-a398-baf7d623ded20.MirrorCS");Q1=makeQuery(id+"F16.imprint","IMPRINT",FACE,{"disambiguationData":[TD([[makeQuery(id+"F16.imprint","IMPRINT",EDGE,{"derivedFrom":subQ3}),1.0]])]});}
            var Q2;
            Q2=makeQuery(id+"F16.imprint","IMPRINT",FACE,{"disambiguationData":[TD([[makeQuery(id+"F16.imprint","IMPRINT",EDGE,{"derivedFrom":makeQuery(id+"F1.opExtrude","CAP_EDGE",EDGE,{"disambiguationData":[OSD([sQuery(id+"F0.wireOp",EDGE,"E1.left")])],"isStart":true})}),-1.0]])]});
            var Q3;
            Q3=makeQuery(id+"F16.imprint","IMPRINT",FACE,{"disambiguationData":[TD([[makeQuery(id+"F16.imprint","IMPRINT",EDGE,{"derivedFrom":sQuery(id+"F16.wireOp",EDGE,"E85.MirrorCS")}),-1.0]])]});
            var Q4;
            Q4=makeQuery(id+"F2.opExtrude","CAP_FACE",FACE,{"disambiguationData":[OSD([sQuery(id+"F0.wireOp",EDGE,"E12"),sQuery(id+"F0.wireOp",EDGE,"E13"),sQuery(id+"F0.wireOp",EDGE,"E14"),sQuery(id+"F0.wireOp",EDGE,"E15"),sQuery(id+"F0.wireOp",EDGE,"E17.filletArc"),sQuery(id+"F0.wireOp",EDGE,"E18.filletArc"),sQuery(id+"F0.wireOp",EDGE,"E19.filletArc"),sQuery(id+"F0.wireOp",EDGE,"E20.filletArc"),sQuery(id+"F0.wireOp",EDGE,"E25.0"),sQuery(id+"F0.wireOp",EDGE,"E25.1"),sQuery(id+"F0.wireOp",EDGE,"E25.2"),sQuery(id+"F0.wireOp",EDGE,"E25.3"),sQuery(id+"F0.wireOp",EDGE,"E25.4"),sQuery(id+"F0.wireOp",EDGE,"E25.5"),sQuery(id+"F0.wireOp",EDGE,"E25.6"),sQuery(id+"F0.wireOp",EDGE,"E25.7")])],"isStart":false});
            extrude(context, id + "F17", {"entities" : qUnion([Q0, Q1, Q2, Q3]), "endBound" : BoundingType.UP_TO_SURFACE, "endBoundEntityFace" : qUnion([Q4]), "depth" : 25 * mm});
        }
    });
